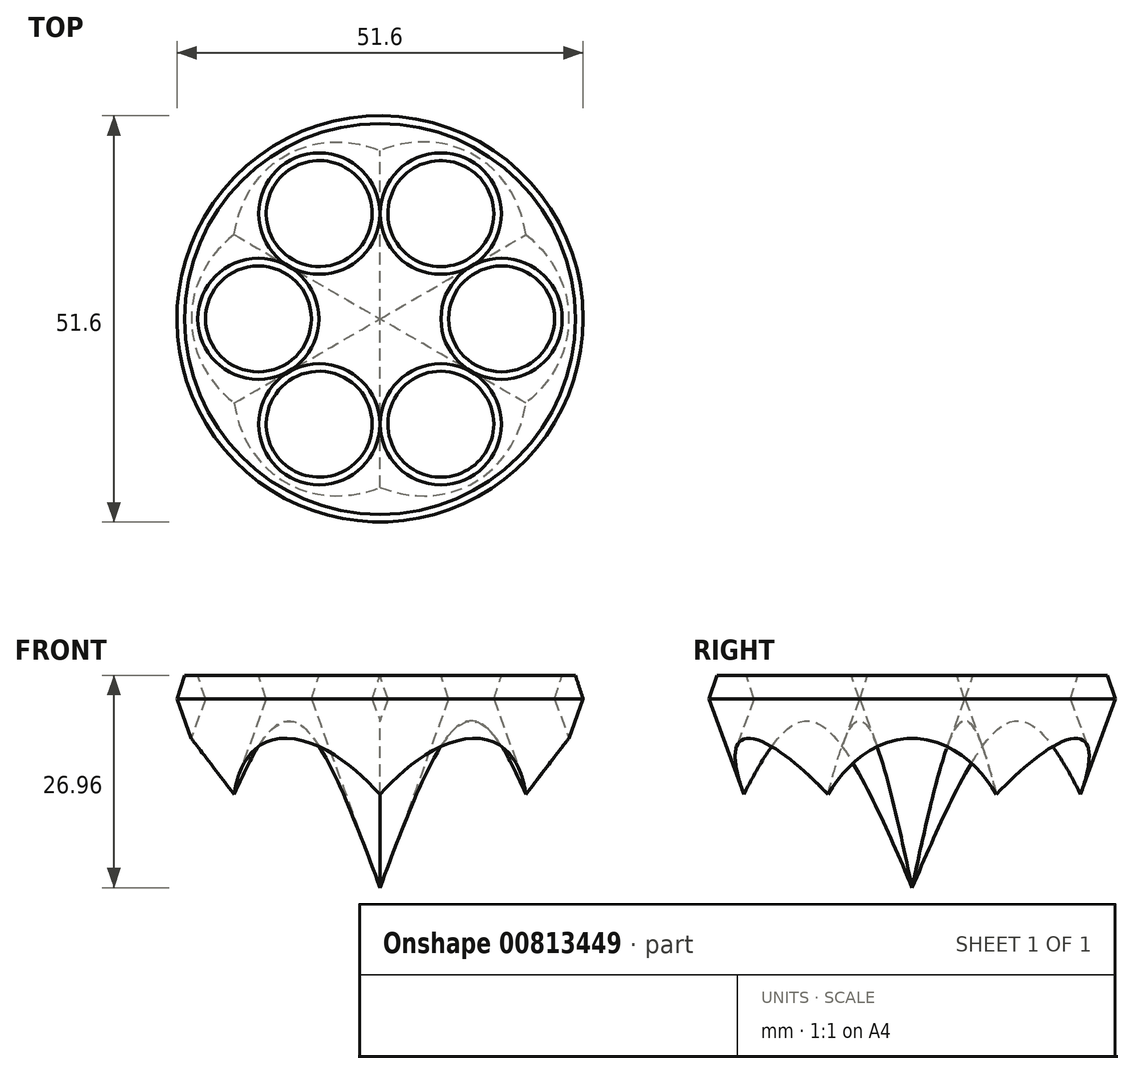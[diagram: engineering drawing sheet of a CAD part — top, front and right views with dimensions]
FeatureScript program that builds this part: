
annotation { "Feature Type Name" : "Feature", "Feature Type Description" : "" }
export const myFeature = defineFeature(function(context is Context, id is Id, definition is map)
    precondition{}
    {
        {
            var Q0;
            Q0=qCreatedBy(makeId("Top.planeOp"),FACE);
            var sketch = newSketch(context, id + "F0", { "sketchPlane" : qUnion([Q0])});
            skCircle(sketch, "E0", {"center": v(0, 0) * mm, "radius": 25.8 * mm});
            skCircle(sketch, "E1", {"center": v(0, 0) * mm, "radius": 15.45 * mm, "construction": true});
            skCircle(sketch, "E2", {"center": v(-15.45, 0) * mm, "radius": 6.73 * mm});
            skCircle(sketch, "E3.1.0", {"center": v(-7.72, -13.38) * mm, "radius": 6.73 * mm});
            skCircle(sketch, "E3.2.0", {"center": v(7.72, -13.38) * mm, "radius": 6.73 * mm});
            skCircle(sketch, "E3.3.0", {"center": v(15.45, 0) * mm, "radius": 6.73 * mm});
            skCircle(sketch, "E3.4.0", {"center": v(7.72, 13.38) * mm, "radius": 6.73 * mm});
            skCircle(sketch, "E3.5.0", {"center": v(-7.72, 13.38) * mm, "radius": 6.73 * mm});
            skSolve(sketch);
        }
        {
            var Q0;
            Q0=makeQuery(id+"F0.imprint","IMPRINT",FACE,{"disambiguationData":[TD([[makeQuery(id+"F0.imprint","IMPRINT",EDGE,{"derivedFrom":sQuery(id+"F0.wireOp",EDGE,"E0")}),1.0]])]});
            extrude(context, id + "F1", {"entities" : qUnion([Q0]), "depth" : 3 * mm, "offsetDistance" : 25.4 * mm, "hasDraft" : true, "draftAngle" : 18 * degree, "draftPullDirection" : true});
        }
        {
            var Q0;
            Q0=makeQuery(id+"F1.opExtrude","CAP_FACE",FACE,{"disambiguationData":[OSD([sQuery(id+"F0.wireOp",EDGE,"E0"),sQuery(id+"F0.wireOp",EDGE,"E2"),sQuery(id+"F0.wireOp",EDGE,"E3.1.0"),sQuery(id+"F0.wireOp",EDGE,"E3.2.0"),sQuery(id+"F0.wireOp",EDGE,"E3.3.0"),sQuery(id+"F0.wireOp",EDGE,"E3.4.0"),sQuery(id+"F0.wireOp",EDGE,"E3.5.0")])],"isStart":true});
            extrude(context, id + "F2", {"entities" : qUnion([Q0]), "operationType" : NewBodyOperationType.ADD, "depth" : 25.4 * mm, "offsetDistance" : 25.4 * mm, "hasDraft" : true, "draftAngle" : 20 * degree, "draftPullDirection" : true});
        }
    });
